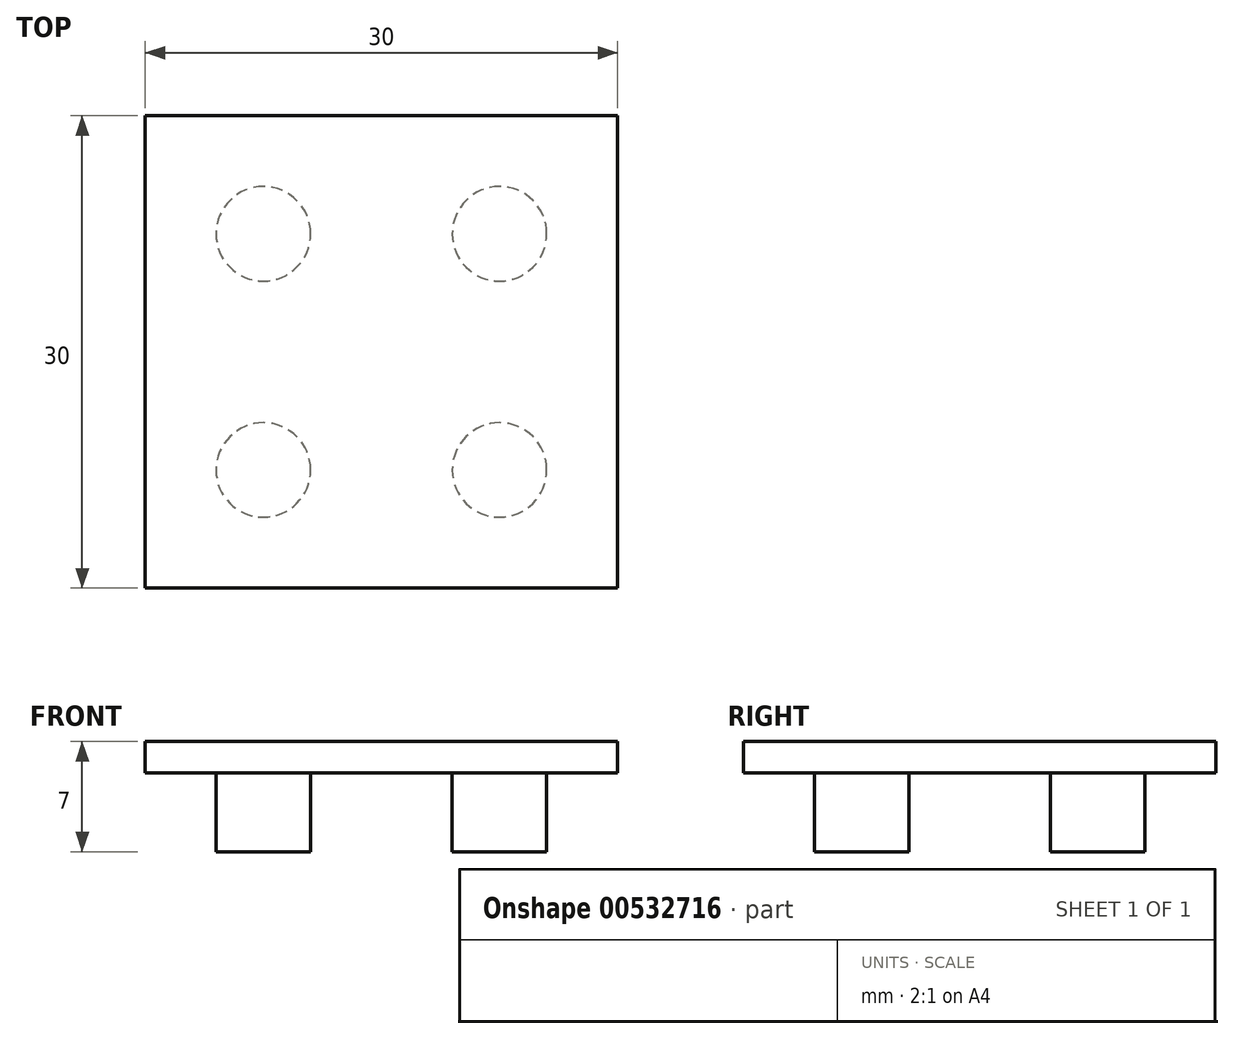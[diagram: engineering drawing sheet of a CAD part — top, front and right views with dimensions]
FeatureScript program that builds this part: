
annotation { "Feature Type Name" : "Feature", "Feature Type Description" : "" }
export const myFeature = defineFeature(function(context is Context, id is Id, definition is map)
    precondition{}
    {
        {
            var Q0;
            Q0=qCreatedBy(makeId("Top.planeOp"),FACE);
            var sketch = newSketch(context, id + "F0", { "sketchPlane" : qUnion([Q0])});
            skLineSegment(sketch, "E0.bottom", {"start": v(15, 15) * mm, "end": v(-15, 15) * mm});
            skLineSegment(sketch, "E0.top", {"start": v(15, -15) * mm, "end": v(-15, -15) * mm});
            skLineSegment(sketch, "E0.left", {"start": v(15, 15) * mm, "end": v(15, -15) * mm});
            skLineSegment(sketch, "E0.right", {"start": v(-15, 15) * mm, "end": v(-15, -15) * mm});
            skPoint(sketch, "E0.middle", {"position": v(0, 0) * mm});
            skSolve(sketch);
        }
        {
            var Q0;
            Q0=makeQuery(id+"F0.imprint","IMPRINT",FACE,{"disambiguationData":[TD([[makeQuery(id+"F0.imprint","IMPRINT",EDGE,{"derivedFrom":sQuery(id+"F0.wireOp",EDGE,"E0.bottom")}),1.0]])]});
            extrude(context, id + "F1", {"entities" : qUnion([Q0]), "depth" : 2 * mm});
        }
        {
            var Q0;
            Q0=qCreatedBy(makeId("Top.planeOp"),FACE);
            var sketch = newSketch(context, id + "F2", { "sketchPlane" : qUnion([Q0])});
            skPoint(sketch, "E1.middle", {"position": v(0, 0) * mm});
            skCircle(sketch, "E2", {"center": v(-7.5, -7.5) * mm, "radius": 3 * mm});
            skCircle(sketch, "E3", {"center": v(7.5, -7.5) * mm, "radius": 3 * mm});
            skCircle(sketch, "E4", {"center": v(-7.5, 7.5) * mm, "radius": 3 * mm});
            skCircle(sketch, "E5", {"center": v(7.5, 7.5) * mm, "radius": 3 * mm});
            skSolve(sketch);
        }
        {
            var Q0;
            Q0=makeQuery(id+"F2.imprint","IMPRINT",FACE,{"disambiguationData":[TD([[makeQuery(id+"F2.imprint","IMPRINT",EDGE,{"derivedFrom":sQuery(id+"F2.wireOp",EDGE,"E2")}),1.0]])]});
            var Q1;
            Q1=makeQuery(id+"F2.imprint","IMPRINT",FACE,{"disambiguationData":[TD([[makeQuery(id+"F2.imprint","IMPRINT",EDGE,{"derivedFrom":sQuery(id+"F2.wireOp",EDGE,"E3")}),1.0]])]});
            var Q2;
            Q2=makeQuery(id+"F2.imprint","IMPRINT",FACE,{"disambiguationData":[TD([[makeQuery(id+"F2.imprint","IMPRINT",EDGE,{"derivedFrom":sQuery(id+"F2.wireOp",EDGE,"E5")}),1.0]])]});
            var Q3;
            Q3=makeQuery(id+"F2.imprint","IMPRINT",FACE,{"disambiguationData":[TD([[makeQuery(id+"F2.imprint","IMPRINT",EDGE,{"derivedFrom":sQuery(id+"F2.wireOp",EDGE,"E4")}),1.0]])]});
            extrude(context, id + "F3", {"entities" : qUnion([Q0, Q1, Q2, Q3]), "operationType" : NewBodyOperationType.ADD, "oppositeDirection" : true, "depth" : 5 * mm});
        }
    });
